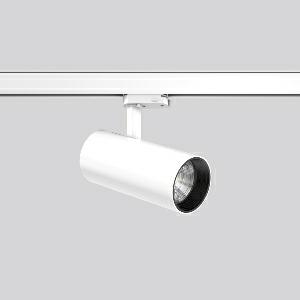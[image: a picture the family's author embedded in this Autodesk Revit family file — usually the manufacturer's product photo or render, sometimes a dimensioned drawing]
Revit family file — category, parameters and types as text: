
# Revit family: deecos_s_mini_742194_002_965c
name_source: partatom
category: Lighting Fixtures
units: mm (PartAtom-declared; Revit-internal decimal feet)

## family parameters
Cut with Voids When Loaded = No
Host = Face
Light Source = No
Part Type = Normal
Room Calculation Point = No
Round Connector Dimension = Use Diameter
Shared = No

## types (1)
- DEECOS S mini (1 x LED Modul 930, 2000 lm, 3000)
    Apparent Load = 22 VA
    Approval mark = CE
    CIE Flux Codes = 99 100 100 100 100
    Color Rendering = 90
    Color Temperature = 3000
    Default Elevation = 1800 mm
    Description = Series: DEECOS S mini
LED surface-mounted projector in modern design with no visible cooling ribs. Housing: die-cast aluminium, powder-coated. Rotation range: 356°. Swivel range: 90°. Black plastic ring and recessed LED to prevent glare from the side. Optical assembly with lens made of plastic (polycarbonate) for the best homogeneous light distribution - can be changed without tools. Best colour rendering index Ra>90. Superspot version with small spot LED. With multi adaptor for 3-circuit tracks 230 V. Suitable for Track on ceiling, Wall track. High quality converter without flickering and stroboscopic effect. The following accessories can be mounted without use of tools: interchangeable lenses, decorative glasses, honeycomb louvre, clear and frosted diffusers, white interchangeable plastic ring. 
Colour: traffic white, matt (RAL 9016)
Diameter: 87 mm
Height: 214 mm
Lamp: LED
Socket: without socket
Colour temperature: 3000K
Colour rendering index (CRI): 92
System power: 22 W
Rated luminous flux: 2000 lm
Luminous efficiency: 91 lm/W
Control gear: Regulated power supply
Protection class: I
Type of protection: IP 20
    Height = 214 mm
    Lamp = 1 x LED Modul 930
    Lamp Light Flux = 2000 lm
    Lamp count = 1
    Length = 87 mm
    Lifetime = 50000 h
    Luminous efficacy = 91 lm/W
    Manufacturer = RZB
    ModVariant = No
    Model = 742194.002
    Mounting Place = Ceiling
    Mounting Type = Rail mounted
    Number of Poles = 1
    OnlyDefault = Yes
    Power Factor = 1
    Product Name = DEECOS S mini
    Product group = Track mounted projectors
    ProductGroupID = 301
    Protection Class = Protection class I
    Protection Degree = IP 20
    RLX_Detail_Level = 1
    RLX_Emergency_Light_Flux = 0 lm
    RLX_Emergency_Type = 0
    RLX_Emergency_Type_DB = No
    RlxData = <blob elided: 35621 chars, md5=5157f405>
    Socket = socket
    Standby Power = 0 W
    System Light Flux = 2000 lm
    System Power = 22 W
    Type Comments = Product without accessories
    Type Image = 741930.002.jpg
    URL = http://relux.com
    VarID = ---
    Voltage = 230 V
    Voltage Range = 220-240 V
    Weight = 0.00 kg
    Width = 0 mm  [stored 0 ft]

note: [stored X ft] marks values corroborated as IEEE doubles in the binary element streams (Revit-internal decimal feet)

## geometry (parser evidence)
native form markers: Blend x4, Sweep x12
no freeform markers — native parametric forms only
